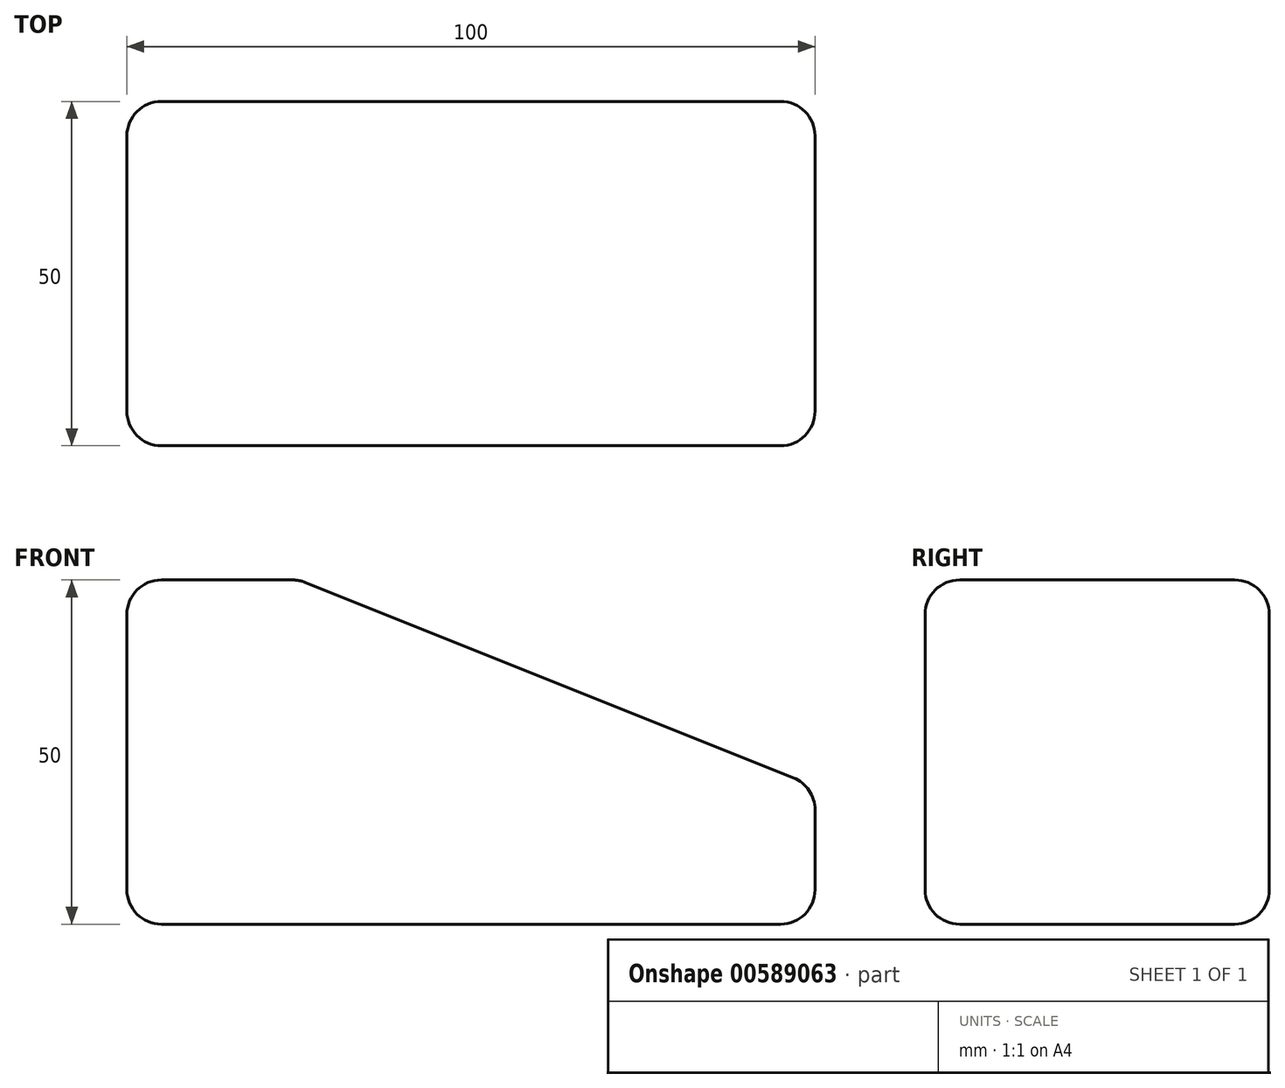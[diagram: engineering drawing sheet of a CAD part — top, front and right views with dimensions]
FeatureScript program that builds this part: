
annotation { "Feature Type Name" : "Feature", "Feature Type Description" : "" }
export const myFeature = defineFeature(function(context is Context, id is Id, definition is map)
    precondition{}
    {
        {
            var Q0;
            Q0=qCreatedBy(makeId("Front.planeOp"),FACE);
            var sketch = newSketch(context, id + "F0", { "sketchPlane" : qUnion([Q0])});
            skLineSegment(sketch, "E0", {"start": v(0, 0) * mm, "end": v(0, 50) * mm});
            skLineSegment(sketch, "E1", {"start": v(0, 50) * mm, "end": v(25, 50) * mm});
            skLineSegment(sketch, "E2", {"start": v(25, 50) * mm, "end": v(100, 20) * mm});
            skLineSegment(sketch, "E3", {"start": v(100, 20) * mm, "end": v(100, 0) * mm});
            skLineSegment(sketch, "E4", {"start": v(0, 0) * mm, "end": v(100, 0) * mm});
            skSolve(sketch);
        }
        {
            var Q0;
            Q0=makeQuery(id+"F0.imprint","IMPRINT",FACE,{"disambiguationData":[TD([[makeQuery(id+"F0.imprint","IMPRINT",EDGE,{"derivedFrom":sQuery(id+"F0.wireOp",EDGE,"E0")}),-1.0]])]});
            extrude(context, id + "F1", {"entities" : qUnion([Q0]), "depth" : 50 * mm, "offsetDistance" : 25 * mm});
        }
        {
            var Q0;
            Q0=makeQuery(id+"F1.opExtrude","SWEPT_FACE",FACE,{"disambiguationData":[OSD([sQuery(id+"F0.wireOp",EDGE,"E2")])]});
            var Q1;
            Q1=makeQuery(id+"F1.opExtrude","SWEPT_FACE",FACE,{"disambiguationData":[OSD([sQuery(id+"F0.wireOp",EDGE,"E1")])]});
            var Q2;
            Q2=makeQuery(id+"F1.opExtrude","SWEPT_FACE",FACE,{"disambiguationData":[OSD([sQuery(id+"F0.wireOp",EDGE,"E3")])]});
            var Q3;
            Q3=makeQuery(id+"F1.opExtrude","CAP_FACE",FACE,{"disambiguationData":[OSD([sQuery(id+"F0.wireOp",EDGE,"E0"),sQuery(id+"F0.wireOp",EDGE,"E1"),sQuery(id+"F0.wireOp",EDGE,"E2"),sQuery(id+"F0.wireOp",EDGE,"E3"),sQuery(id+"F0.wireOp",EDGE,"E4")])],"isStart":true});
            var Q4;
            Q4=makeQuery(id+"F1.opExtrude","CAP_FACE",FACE,{"disambiguationData":[OSD([sQuery(id+"F0.wireOp",EDGE,"E0"),sQuery(id+"F0.wireOp",EDGE,"E1"),sQuery(id+"F0.wireOp",EDGE,"E2"),sQuery(id+"F0.wireOp",EDGE,"E3"),sQuery(id+"F0.wireOp",EDGE,"E4")])],"isStart":false});
            var Q5;
            Q5=makeQuery(id+"F1.opExtrude","SWEPT_FACE",FACE,{"disambiguationData":[OSD([sQuery(id+"F0.wireOp",EDGE,"E4")])]});
            fillet(context, id + "F2", {"entities" : qUnion([Q0, Q1, Q2, Q3, Q4, Q5]), "radius" : 5 * mm, "tangentPropagation" : true, "allowEdgeOverflow" : false});
        }
    });
